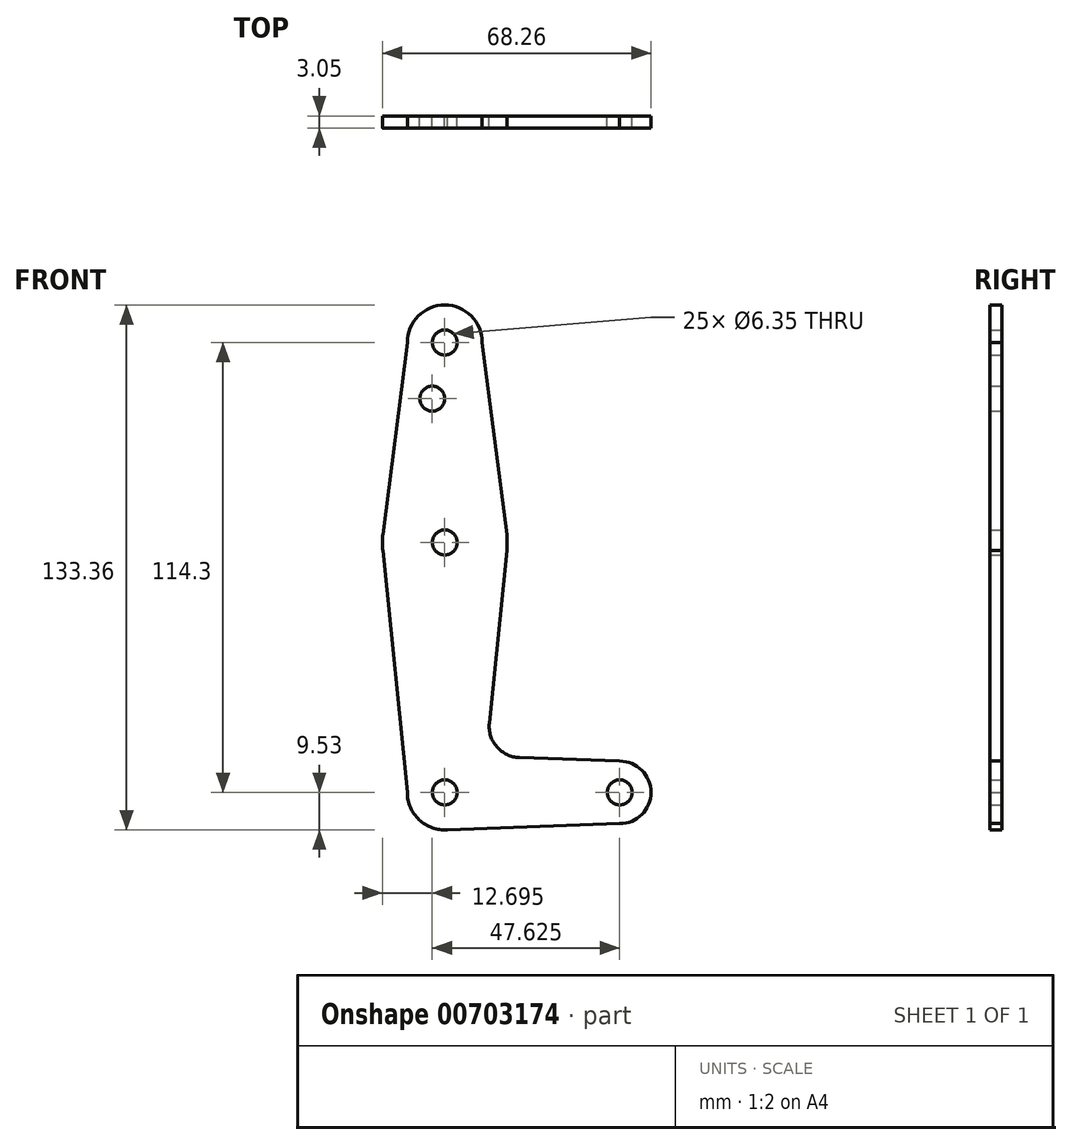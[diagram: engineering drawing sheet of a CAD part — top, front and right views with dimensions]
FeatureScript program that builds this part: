
annotation { "Feature Type Name" : "Feature", "Feature Type Description" : "" }
export const myFeature = defineFeature(function(context is Context, id is Id, definition is map)
    precondition{}
    {
        {
            var Q0;
            Q0=qCreatedBy(makeId("Front.planeOp"),FACE);
            var sketch = newSketch(context, id + "F0", { "sketchPlane" : qUnion([Q0])});
            skLineSegment(sketch, "E0", {"start": v(0, 0) * mm, "end": v(0, 114.3) * mm});
            skLineSegment(sketch, "E1", {"start": v(0, 0) * mm, "end": v(44.45, 0) * mm});
            skCircle(sketch, "E2", {"center": v(0, 114.3) * mm, "radius": 9.53 * mm});
            skCircle(sketch, "E3", {"center": v(0, 63.5) * mm, "radius": 15.88 * mm});
            skCircle(sketch, "E4", {"center": v(0, 0) * mm, "radius": 9.53 * mm});
            skCircle(sketch, "E5", {"center": v(44.45, 0) * mm, "radius": 7.94 * mm});
            skCircle(sketch, "E6", {"center": v(-3.18, 100.03) * mm, "radius": 3.18 * mm});
            skCircle(sketch, "E7", {"center": v(0, 114.3) * mm, "radius": 3.18 * mm});
            skCircle(sketch, "E8", {"center": v(0, 63.5) * mm, "radius": 3.18 * mm});
            skCircle(sketch, "E9", {"center": v(0, 0) * mm, "radius": 3.18 * mm});
            skCircle(sketch, "E10", {"center": v(44.45, 0) * mm, "radius": 3.18 * mm});
            skLineSegment(sketch, "E11", {"start": v(9.52, 114.3) * mm, "end": v(15.75, 65.5) * mm});
            skLineSegment(sketch, "E12", {"start": v(-9.53, 114.3) * mm, "end": v(-15.75, 65.5) * mm});
            skLineSegment(sketch, "E13", {"start": v(-15.75, 61.5) * mm, "end": v(-9.52, 0) * mm});
            skLineSegment(sketch, "E14", {"start": v(15.75, 61.5) * mm, "end": v(11.3, 17.6) * mm});
            skLineSegment(sketch, "E15", {"start": v(18.93, 8.85) * mm, "end": v(44.45, 7.94) * mm});
            skLineSegment(sketch, "E16", {"start": v(0, -9.52) * mm, "end": v(44.45, -7.94) * mm});
            skArc(sketch, "E17.filletArc", {"start": v(11.3, 17.6) * mm, "mid": v(13.22, 11.57) * mm, "end": v(18.93, 8.85) * mm});
            skSolve(sketch);
        }
        {
            var Q0;
            Q0 = qSketchRegion(id + "F0", true);
            var Q1;
            {var subQ0=sQuery(id+"F0.wireOp",EDGE,"E9");var subQ1=sQuery(id+"F0.wireOp",EDGE,"E0");var subQ2=makeQuery(id+"F0.imprint","INTERSECT",VERTEX,{"derivedFrom":[subQ1,subQ0]});Q1=makeQuery(id+"F0.imprint","IMPRINT",FACE,{"disambiguationData":[TD([[makeQuery(id+"F0.imprint","IMPRINT",EDGE,{"disambiguationData":[TD([[subQ2,-1.0]])],"derivedFrom":subQ1}),-1.0]])]});}
            extrude(context, id + "F1", {"entities" : qUnion([Q0, Q1]), "depth" : 3.05 * mm, "offsetDistance" : 25.4 * mm});
        }
    });
